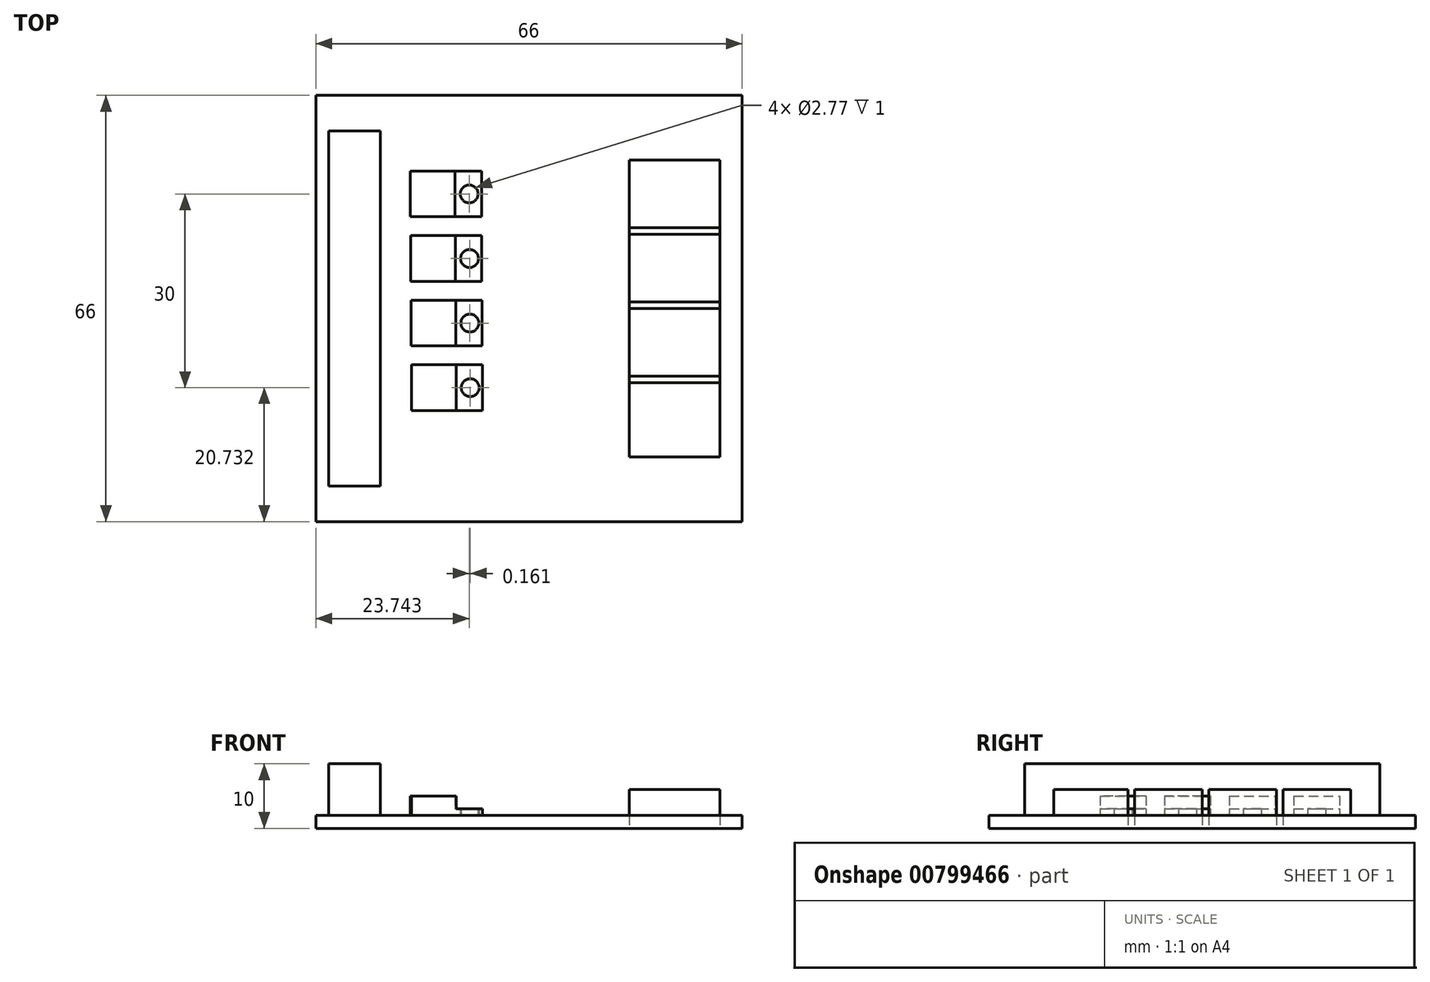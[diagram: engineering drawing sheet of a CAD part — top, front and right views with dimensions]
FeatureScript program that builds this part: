
annotation { "Feature Type Name" : "Feature", "Feature Type Description" : "" }
export const myFeature = defineFeature(function(context is Context, id is Id, definition is map)
    precondition{}
    {
        {
            var Q0;
            Q0=qCreatedBy(makeId("Top.planeOp"),FACE);
            var sketch = newSketch(context, id + "F0", { "sketchPlane" : qUnion([Q0])});
            skLineSegment(sketch, "E0.bottom", {"start": v(0, 0) * mm, "end": v(66, 0) * mm});
            skLineSegment(sketch, "E0.top", {"start": v(0, 66) * mm, "end": v(66, 66) * mm});
            skLineSegment(sketch, "E0.left", {"start": v(0, 0) * mm, "end": v(0, 66) * mm});
            skLineSegment(sketch, "E0.right", {"start": v(66, 0) * mm, "end": v(66, 66) * mm});
            skLineSegment(sketch, "E1.bottom", {"start": v(48.56, 56) * mm, "end": v(62.56, 56) * mm});
            skLineSegment(sketch, "E1.top", {"start": v(48.56, 10) * mm, "end": v(62.56, 10) * mm});
            skLineSegment(sketch, "E1.left", {"start": v(48.56, 56) * mm, "end": v(48.56, 10) * mm});
            skLineSegment(sketch, "E1.right", {"start": v(62.56, 56) * mm, "end": v(62.56, 10) * mm});
            skLineSegment(sketch, "E2", {"start": v(48.56, 33) * mm, "end": v(62.56, 33) * mm});
            skLineSegment(sketch, "E3", {"start": v(62.56, 44.5) * mm, "end": v(48.56, 44.5) * mm});
            skLineSegment(sketch, "E4", {"start": v(62.56, 21.5) * mm, "end": v(48.56, 21.5) * mm});
            skLineSegment(sketch, "E5.0", {"start": v(62.56, 45.5) * mm, "end": v(48.56, 45.5) * mm});
            skLineSegment(sketch, "E6.0", {"start": v(48.56, 34) * mm, "end": v(62.56, 34) * mm});
            skLineSegment(sketch, "E7.0", {"start": v(62.56, 22.5) * mm, "end": v(48.56, 22.5) * mm});
            skLineSegment(sketch, "E8.bottom", {"start": v(2, 60.5) * mm, "end": v(10, 60.5) * mm});
            skLineSegment(sketch, "E8.top", {"start": v(2, 5.5) * mm, "end": v(10, 5.5) * mm});
            skLineSegment(sketch, "E8.left", {"start": v(2, 60.5) * mm, "end": v(2, 5.5) * mm});
            skLineSegment(sketch, "E8.right", {"start": v(10, 60.5) * mm, "end": v(10, 5.5) * mm});
            skLineSegment(sketch, "E9.bottom", {"start": v(14.64, 47.19) * mm, "end": v(25.65, 47.19) * mm});
            skLineSegment(sketch, "E9.top", {"start": v(14.64, 54.28) * mm, "end": v(25.65, 54.28) * mm});
            skLineSegment(sketch, "E9.left", {"start": v(14.64, 47.19) * mm, "end": v(14.64, 54.28) * mm});
            skLineSegment(sketch, "E9.right", {"start": v(25.65, 47.19) * mm, "end": v(25.65, 54.28) * mm});
            skLineSegment(sketch, "E10", {"start": v(21.58, 54.28) * mm, "end": v(21.58, 47.19) * mm});
            skCircle(sketch, "E11", {"center": v(23.74, 50.73) * mm, "radius": 1.39 * mm});
            skLineSegment(sketch, "E12.1.0.0", {"start": v(14.7, 37.19) * mm, "end": v(25.7, 37.19) * mm});
            skLineSegment(sketch, "E12.1.0.1", {"start": v(25.7, 37.19) * mm, "end": v(25.7, 44.28) * mm});
            skLineSegment(sketch, "E12.1.0.2", {"start": v(14.7, 44.28) * mm, "end": v(25.7, 44.28) * mm});
            skLineSegment(sketch, "E12.1.0.3", {"start": v(14.7, 37.19) * mm, "end": v(14.7, 44.28) * mm});
            skLineSegment(sketch, "E12.1.0.4", {"start": v(21.63, 44.28) * mm, "end": v(21.63, 37.19) * mm});
            skCircle(sketch, "E12.1.0.5", {"center": v(23.8, 40.73) * mm, "radius": 1.39 * mm});
            skLineSegment(sketch, "E12.2.0.0", {"start": v(14.75, 27.19) * mm, "end": v(25.76, 27.19) * mm});
            skLineSegment(sketch, "E12.2.0.1", {"start": v(25.76, 27.19) * mm, "end": v(25.76, 34.28) * mm});
            skLineSegment(sketch, "E12.2.0.2", {"start": v(14.75, 34.28) * mm, "end": v(25.76, 34.28) * mm});
            skLineSegment(sketch, "E12.2.0.3", {"start": v(14.75, 27.19) * mm, "end": v(14.75, 34.28) * mm});
            skLineSegment(sketch, "E12.2.0.4", {"start": v(21.68, 34.28) * mm, "end": v(21.68, 27.19) * mm});
            skCircle(sketch, "E12.2.0.5", {"center": v(23.85, 30.73) * mm, "radius": 1.39 * mm});
            skLineSegment(sketch, "E12.3.0.0", {"start": v(14.8, 17.19) * mm, "end": v(25.8, 17.19) * mm});
            skLineSegment(sketch, "E12.3.0.1", {"start": v(25.8, 17.19) * mm, "end": v(25.8, 24.28) * mm});
            skLineSegment(sketch, "E12.3.0.2", {"start": v(14.8, 24.28) * mm, "end": v(25.8, 24.28) * mm});
            skLineSegment(sketch, "E12.3.0.3", {"start": v(14.8, 17.19) * mm, "end": v(14.8, 24.28) * mm});
            skLineSegment(sketch, "E12.3.0.4", {"start": v(21.74, 24.28) * mm, "end": v(21.74, 17.19) * mm});
            skCircle(sketch, "E12.3.0.5", {"center": v(23.9, 20.73) * mm, "radius": 1.39 * mm});
            skLineSegment(sketch, "E12.direction1", {"start": v(14.64, 47.19) * mm, "end": v(14.7, 37.19) * mm, "construction": true});
            skSolve(sketch);
        }
        {
            var Q0;
            Q0=makeQuery(id+"F0.imprint","IMPRINT",FACE,{"disambiguationData":[TD([[makeQuery(id+"F0.imprint","IMPRINT",EDGE,{"derivedFrom":sQuery(id+"F0.wireOp",EDGE,"E0.bottom")}),1.0]])]});
            extrude(context, id + "F1", {"entities" : qUnion([Q0]), "depth" : 2 * mm, "offsetDistance" : 25 * mm});
        }
        {
            var Q0;
            {var subQ0=sQuery(id+"F0.wireOp",EDGE,"E1.bottom");Q0=makeQuery(id+"F0.imprint","IMPRINT",FACE,{"disambiguationData":[TD([[makeQuery(id+"F0.imprint","IMPRINT",EDGE,{"derivedFrom":subQ0}),-1.0]])]});}
            var Q1;
            {var subQ0=sQuery(id+"F0.wireOp",EDGE,"E3");Q1=makeQuery(id+"F0.imprint","IMPRINT",FACE,{"disambiguationData":[TD([[makeQuery(id+"F0.imprint","IMPRINT",EDGE,{"derivedFrom":subQ0}),1.0]])]});}
            var Q2;
            {var subQ0=sQuery(id+"F0.wireOp",EDGE,"E2");Q2=makeQuery(id+"F0.imprint","IMPRINT",FACE,{"disambiguationData":[TD([[makeQuery(id+"F0.imprint","IMPRINT",EDGE,{"derivedFrom":subQ0}),-1.0]])]});}
            var Q3;
            {var subQ0=sQuery(id+"F0.wireOp",EDGE,"E1.top");Q3=makeQuery(id+"F0.imprint","IMPRINT",FACE,{"disambiguationData":[TD([[makeQuery(id+"F0.imprint","IMPRINT",EDGE,{"derivedFrom":subQ0}),1.0]])]});}
            extrude(context, id + "F2", {"entities" : qUnion([Q0, Q1, Q2, Q3]), "operationType" : NewBodyOperationType.ADD, "depth" : 6 * mm, "offsetDistance" : 25 * mm});
        }
        {
            var Q0;
            Q0=makeQuery(id+"F0.imprint","IMPRINT",FACE,{"disambiguationData":[TD([[makeQuery(id+"F0.imprint","IMPRINT",EDGE,{"derivedFrom":sQuery(id+"F0.wireOp",EDGE,"E8.bottom")}),-1.0]])]});
            extrude(context, id + "F3", {"entities" : qUnion([Q0]), "operationType" : NewBodyOperationType.ADD, "depth" : 10 * mm, "offsetDistance" : 25 * mm});
        }
        {
            var Q0;
            {var subQ0=sQuery(id+"F0.wireOp",EDGE,"E9.right");Q0=makeQuery(id+"F0.imprint","IMPRINT",FACE,{"disambiguationData":[TD([[makeQuery(id+"F0.imprint","IMPRINT",EDGE,{"derivedFrom":subQ0}),1.0]])]});}
            var Q1;
            {var subQ1=sQuery(id+"F0.wireOp",EDGE,"E12.1.0.1");Q1=makeQuery(id+"F0.imprint","IMPRINT",FACE,{"disambiguationData":[TD([[makeQuery(id+"F0.imprint","IMPRINT",EDGE,{"derivedFrom":subQ1}),1.0]])]});}
            var Q2;
            {var subQ1=sQuery(id+"F0.wireOp",EDGE,"E12.2.0.1");Q2=makeQuery(id+"F0.imprint","IMPRINT",FACE,{"disambiguationData":[TD([[makeQuery(id+"F0.imprint","IMPRINT",EDGE,{"derivedFrom":subQ1}),1.0]])]});}
            var Q3;
            {var subQ1=sQuery(id+"F0.wireOp",EDGE,"E12.3.0.1");Q3=makeQuery(id+"F0.imprint","IMPRINT",FACE,{"disambiguationData":[TD([[makeQuery(id+"F0.imprint","IMPRINT",EDGE,{"derivedFrom":subQ1}),1.0]])]});}
            extrude(context, id + "F4", {"entities" : qUnion([Q0, Q1, Q2, Q3]), "operationType" : NewBodyOperationType.ADD, "depth" : 3 * mm, "offsetDistance" : 25 * mm});
        }
        {
            var Q0;
            {var subQ0=sQuery(id+"F0.wireOp",EDGE,"E9.left");Q0=makeQuery(id+"F0.imprint","IMPRINT",FACE,{"disambiguationData":[TD([[makeQuery(id+"F0.imprint","IMPRINT",EDGE,{"derivedFrom":subQ0}),-1.0]])]});}
            var Q1;
            {var subQ0=sQuery(id+"F0.wireOp",EDGE,"E12.1.0.3");Q1=makeQuery(id+"F0.imprint","IMPRINT",FACE,{"disambiguationData":[TD([[makeQuery(id+"F0.imprint","IMPRINT",EDGE,{"derivedFrom":subQ0}),-1.0]])]});}
            var Q2;
            {var subQ0=sQuery(id+"F0.wireOp",EDGE,"E12.2.0.3");Q2=makeQuery(id+"F0.imprint","IMPRINT",FACE,{"disambiguationData":[TD([[makeQuery(id+"F0.imprint","IMPRINT",EDGE,{"derivedFrom":subQ0}),-1.0]])]});}
            var Q3;
            {var subQ0=sQuery(id+"F0.wireOp",EDGE,"E12.3.0.3");Q3=makeQuery(id+"F0.imprint","IMPRINT",FACE,{"disambiguationData":[TD([[makeQuery(id+"F0.imprint","IMPRINT",EDGE,{"derivedFrom":subQ0}),-1.0]])]});}
            extrude(context, id + "F5", {"entities" : qUnion([Q0, Q1, Q2, Q3]), "operationType" : NewBodyOperationType.ADD, "depth" : 5 * mm, "offsetDistance" : 25 * mm});
        }
        {
            var Q0;
            Q0=makeQuery(id+"F0.imprint","IMPRINT",FACE,{"disambiguationData":[TD([[makeQuery(id+"F0.imprint","IMPRINT",EDGE,{"derivedFrom":sQuery(id+"F0.wireOp",EDGE,"E11")}),1.0]])]});
            var Q1;
            Q1=makeQuery(id+"F0.imprint","IMPRINT",FACE,{"disambiguationData":[TD([[makeQuery(id+"F0.imprint","IMPRINT",EDGE,{"derivedFrom":sQuery(id+"F0.wireOp",EDGE,"E12.1.0.5")}),1.0]])]});
            var Q2;
            Q2=makeQuery(id+"F0.imprint","IMPRINT",FACE,{"disambiguationData":[TD([[makeQuery(id+"F0.imprint","IMPRINT",EDGE,{"derivedFrom":sQuery(id+"F0.wireOp",EDGE,"E12.2.0.5")}),1.0]])]});
            var Q3;
            Q3=makeQuery(id+"F0.imprint","IMPRINT",FACE,{"disambiguationData":[TD([[makeQuery(id+"F0.imprint","IMPRINT",EDGE,{"derivedFrom":sQuery(id+"F0.wireOp",EDGE,"E12.3.0.5")}),1.0]])]});
            extrude(context, id + "F6", {"entities" : qUnion([Q0, Q1, Q2, Q3]), "operationType" : NewBodyOperationType.ADD, "depth" : 2 * mm, "offsetDistance" : 25 * mm});
        }
    });
